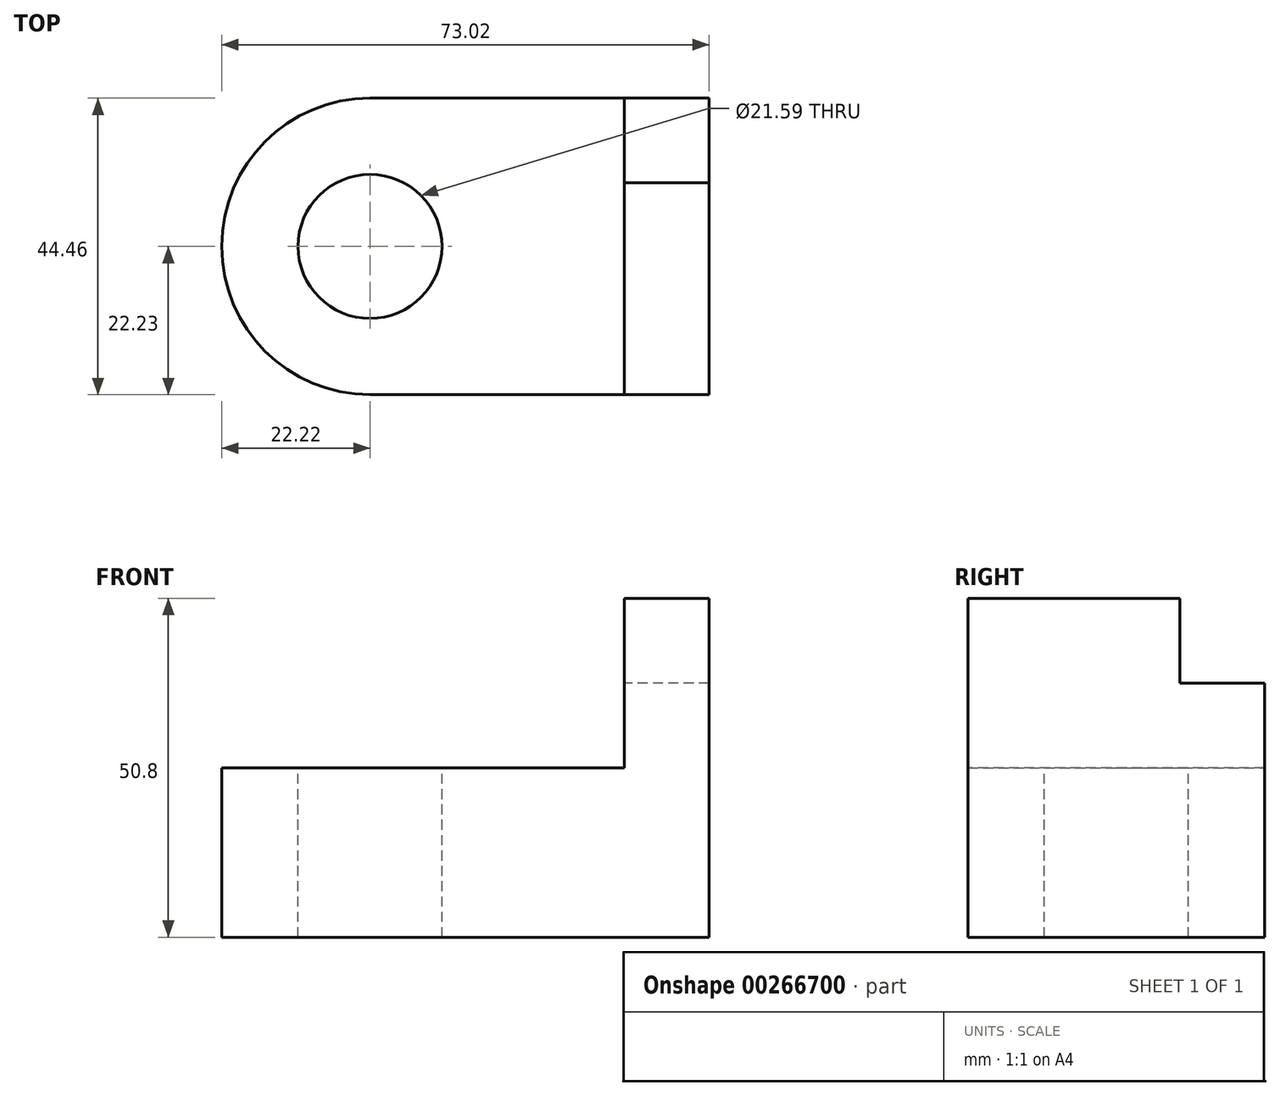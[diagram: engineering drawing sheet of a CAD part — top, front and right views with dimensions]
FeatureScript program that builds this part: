
annotation { "Feature Type Name" : "Feature", "Feature Type Description" : "" }
export const myFeature = defineFeature(function(context is Context, id is Id, definition is map)
    precondition{}
    {
        {
            var Q0;
            Q0=qCreatedBy(makeId("Top.planeOp"),FACE);
            var sketch = newSketch(context, id + "F0", { "sketchPlane" : qUnion([Q0])});
            skLineSegment(sketch, "E0.bottom", {"start": v(25.4, 22.23) * mm, "end": v(-25.4, 22.23) * mm});
            skLineSegment(sketch, "E0.top", {"start": v(25.4, -22.23) * mm, "end": v(-25.4, -22.23) * mm});
            skLineSegment(sketch, "E0.left", {"start": v(25.4, 22.23) * mm, "end": v(25.4, -22.23) * mm});
            skLineSegment(sketch, "E0.right", {"start": v(-25.4, 22.23) * mm, "end": v(-25.4, -22.23) * mm});
            skPoint(sketch, "E0.middle", {"position": v(0, 0) * mm});
            skSolve(sketch);
        }
        {
            var Q0;
            Q0=makeQuery(id+"F0.imprint","IMPRINT",FACE,{"disambiguationData":[TD([[makeQuery(id+"F0.imprint","IMPRINT",EDGE,{"derivedFrom":sQuery(id+"F0.wireOp",EDGE,"E0.bottom")}),1.0]])]});
            extrude(context, id + "F1", {"entities" : qUnion([Q0]), "depth" : 25.4 * mm});
        }
        {
            var Q0;
            Q0=qCreatedBy(makeId("Top.planeOp"),FACE);
            var sketch = newSketch(context, id + "F2", { "sketchPlane" : qUnion([Q0])});
            skCircle(sketch, "E1", {"center": v(-25.4, 0) * mm, "radius": 22.22 * mm});
            skSolve(sketch);
        }
        {
            var Q0;
            Q0=makeQuery(id+"F2.imprint","IMPRINT",FACE,{"disambiguationData":[TD([[makeQuery(id+"F2.imprint","IMPRINT",EDGE,{"derivedFrom":sQuery(id+"F2.wireOp",EDGE,"E1")}),1.0]])]});
            extrude(context, id + "F3", {"entities" : qUnion([Q0]), "operationType" : NewBodyOperationType.ADD, "depth" : 25.4 * mm});
        }
        {
            var Q0;
            Q0=makeQuery(id+"F3.boolean.opBoolean","MERGE",FACE,{"derivedFrom":[makeQuery(id+"F1.opExtrude","CAP_FACE",FACE,{"disambiguationData":[OSD([sQuery(id+"F0.wireOp",EDGE,"E0.bottom"),sQuery(id+"F0.wireOp",EDGE,"E0.top"),sQuery(id+"F0.wireOp",EDGE,"E0.left"),sQuery(id+"F0.wireOp",EDGE,"E0.right")])],"isStart":false}),makeQuery(id+"F3.opExtrude","CAP_FACE",FACE,{"disambiguationData":[OSD([sQuery(id+"F2.wireOp",EDGE,"E1")])],"isStart":false})]});
            var sketch = newSketch(context, id + "F4", { "sketchPlane" : qUnion([Q0])});
            skCircle(sketch, "E2", {"center": v(-25.4, 0) * mm, "radius": 10.8 * mm});
            skSolve(sketch);
        }
        {
            var Q0;
            Q0=makeQuery(id+"F4.imprint","IMPRINT",FACE,{"disambiguationData":[TD([[makeQuery(id+"F4.imprint","IMPRINT",EDGE,{"derivedFrom":sQuery(id+"F4.wireOp",EDGE,"E2")}),1.0]])]});
            extrude(context, id + "F5", {"entities" : qUnion([Q0]), "operationType" : NewBodyOperationType.REMOVE, "endBound" : BoundingType.THROUGH_ALL, "oppositeDirection" : true, "depth" : 25.4 * mm});
        }
        {
            var Q0;
            Q0=makeQuery(id+"F3.boolean.opBoolean","MERGE",FACE,{"derivedFrom":[makeQuery(id+"F1.opExtrude","CAP_FACE",FACE,{"disambiguationData":[OSD([sQuery(id+"F0.wireOp",EDGE,"E0.bottom"),sQuery(id+"F0.wireOp",EDGE,"E0.top"),sQuery(id+"F0.wireOp",EDGE,"E0.left"),sQuery(id+"F0.wireOp",EDGE,"E0.right")])],"isStart":false}),makeQuery(id+"F3.opExtrude","CAP_FACE",FACE,{"disambiguationData":[OSD([sQuery(id+"F2.wireOp",EDGE,"E1")])],"isStart":false})]});
            var sketch = newSketch(context, id + "F6", { "sketchPlane" : qUnion([Q0])});
            skLineSegment(sketch, "E3.bottom", {"start": v(25.4, -22.23) * mm, "end": v(12.7, -22.23) * mm});
            skLineSegment(sketch, "E3.top", {"start": v(25.4, 22.23) * mm, "end": v(12.7, 22.23) * mm});
            skLineSegment(sketch, "E3.left", {"start": v(25.4, -22.23) * mm, "end": v(25.4, 22.23) * mm});
            skLineSegment(sketch, "E3.right", {"start": v(12.7, -22.23) * mm, "end": v(12.7, 22.23) * mm});
            skSolve(sketch);
        }
        {
            var Q0;
            Q0=makeQuery(id+"F6.imprint","IMPRINT",FACE,{"disambiguationData":[TD([[makeQuery(id+"F6.imprint","IMPRINT",EDGE,{"derivedFrom":sQuery(id+"F6.wireOp",EDGE,"E3.bottom")}),-1.0]])]});
            extrude(context, id + "F7", {"entities" : qUnion([Q0]), "operationType" : NewBodyOperationType.ADD, "depth" : 25.4 * mm});
        }
        {
            var Q0;
            Q0=makeQuery(id+"F7.opExtrude","CAP_FACE",FACE,{"disambiguationData":[OSD([sQuery(id+"F6.wireOp",EDGE,"E3.bottom"),sQuery(id+"F6.wireOp",EDGE,"E3.top"),sQuery(id+"F6.wireOp",EDGE,"E3.left"),sQuery(id+"F6.wireOp",EDGE,"E3.right")])],"isStart":false});
            var sketch = newSketch(context, id + "F8", { "sketchPlane" : qUnion([Q0])});
            skLineSegment(sketch, "E4.bottom", {"start": v(12.7, 22.23) * mm, "end": v(25.4, 22.23) * mm});
            skLineSegment(sketch, "E4.top", {"start": v(12.7, 9.53) * mm, "end": v(25.4, 9.53) * mm});
            skLineSegment(sketch, "E4.left", {"start": v(12.7, 22.23) * mm, "end": v(12.7, 9.53) * mm});
            skLineSegment(sketch, "E4.right", {"start": v(25.4, 22.23) * mm, "end": v(25.4, 9.53) * mm});
            skSolve(sketch);
        }
        {
            var Q0;
            Q0=makeQuery(id+"F8.imprint","IMPRINT",FACE,{"disambiguationData":[TD([[makeQuery(id+"F8.imprint","IMPRINT",EDGE,{"derivedFrom":sQuery(id+"F8.wireOp",EDGE,"E4.bottom")}),1.0]])]});
            extrude(context, id + "F9", {"entities" : qUnion([Q0]), "operationType" : NewBodyOperationType.REMOVE, "oppositeDirection" : true, "depth" : 12.7 * mm});
        }
    });
